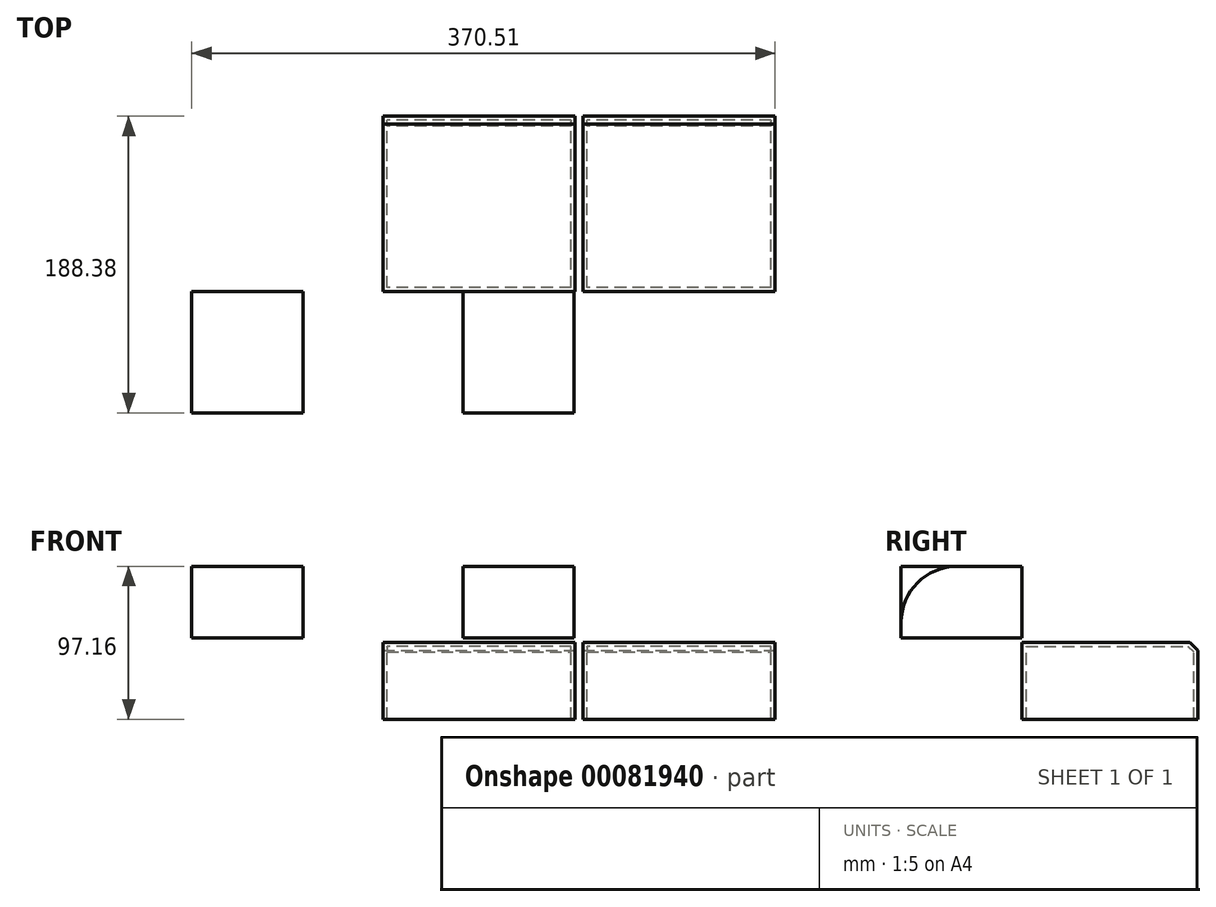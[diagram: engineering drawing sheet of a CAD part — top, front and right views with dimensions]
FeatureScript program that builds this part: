
annotation { "Feature Type Name" : "Feature", "Feature Type Description" : "" }
export const myFeature = defineFeature(function(context is Context, id is Id, definition is map)
    precondition{}
    {
        {
            var Q0;
            Q0=qCreatedBy(makeId("Right.planeOp"),FACE);
            var sketch = newSketch(context, id + "F0", { "sketchPlane" : qUnion([Q0])});
            skLineSegment(sketch, "E0.bottom", {"start": v(0, 0) * mm, "end": v(111.46, 0) * mm});
            skLineSegment(sketch, "E0.top", {"start": v(0, 48.95) * mm, "end": v(111.46, 48.95) * mm});
            skLineSegment(sketch, "E0.left", {"start": v(0, 0) * mm, "end": v(0, 48.95) * mm});
            skLineSegment(sketch, "E0.right", {"start": v(111.46, 0) * mm, "end": v(111.46, 48.95) * mm});
            skSolve(sketch);
        }
        {
            var Q0;
            Q0=qSketchRegion(id+"F0",true);
            extrude(context, id + "F1", {"entities" : qUnion([Q0]), "depth" : 122.06 * mm});
        }
        {
            var Q0;
            Q0=makeQuery(id+"F1.opExtrude","SWEPT_EDGE",EDGE,{"disambiguationData":[OSD([sQuery(id+"F0.wireOp",EDGE,"E0.top"),sQuery(id+"F0.wireOp",EDGE,"E0.right")])]});
            chamfer(context, id + "F2", {"entities" : qUnion([Q0]), "width" : 5.08 * mm, "tangentPropagation" : true});
        }
        {
            var Q0;
            Q0=makeQuery(id+"F1.opExtrude","SWEPT_FACE",FACE,{"disambiguationData":[OSD([sQuery(id+"F0.wireOp",EDGE,"E0.bottom")])]});
            shell(context, id + "F3", {"entities" : qUnion([Q0]), "thickness" : 2.54 * mm});
        }
        {
            var Q0;
            Q0=qCreatedBy(makeId("Front.planeOp"),FACE);
            var sketch = newSketch(context, id + "F4", { "sketchPlane" : qUnion([Q0])});
            skLineSegment(sketch, "E1.bottom", {"start": v(-50.88, 51.58) * mm, "end": v(-121.45, 51.58) * mm});
            skLineSegment(sketch, "E1.top", {"start": v(-50.88, 97.16) * mm, "end": v(-121.45, 97.16) * mm});
            skLineSegment(sketch, "E1.left", {"start": v(-50.88, 51.58) * mm, "end": v(-50.88, 97.16) * mm});
            skLineSegment(sketch, "E1.right", {"start": v(-121.45, 51.58) * mm, "end": v(-121.45, 97.16) * mm});
            skSolve(sketch);
        }
        {
            var Q0;
            Q0=makeQuery(id+"F4.imprint","IMPRINT",FACE,{"disambiguationData":[TD([[makeQuery(id+"F4.imprint","IMPRINT",EDGE,{"derivedFrom":sQuery(id+"F4.wireOp",EDGE,"E1.bottom")}),-1.0]])]});
            extrude(context, id + "F5", {"entities" : qUnion([Q0]), "depth" : 76.92 * mm});
        }
        {
            var Q0;
            Q0=makeQuery(id+"F5.opExtrude","SWEPT_BODY",BODY,{"disambiguationData":[OSD([sQuery(id+"F4.wireOp",EDGE,"E1.bottom"),sQuery(id+"F4.wireOp",EDGE,"E1.top"),sQuery(id+"F4.wireOp",EDGE,"E1.left"),sQuery(id+"F4.wireOp",EDGE,"E1.right")])]});
            var Q1;
            Q1=qCreatedBy(makeId("Right.planeOp"),FACE);
            mirror(context, id + "F6", {"entities" : qUnion([Q0]), "mirrorPlane" : qUnion([Q1])});
        }
        {
            var Q0;
            Q0=makeQuery(id+"F1.opExtrude","SWEPT_BODY",BODY,{"disambiguationData":[OSD([sQuery(id+"F0.wireOp",EDGE,"E0.bottom"),sQuery(id+"F0.wireOp",EDGE,"E0.top"),sQuery(id+"F0.wireOp",EDGE,"E0.left"),sQuery(id+"F0.wireOp",EDGE,"E0.right")])]});
            transform(context, id + "F7", {"entities" : qUnion([Q0]), "transformType" : TransformType.TRANSLATION_3D, "dx" : 127 * mm, "dy" : 0 * mm, "dz" : 0 * mm, "makeCopy" : true});
        }
        {
            var Q0;
            Q0=makeQuery(id+"F6.opPattern","COPY",EDGE,{"derivedFrom":makeQuery(id+"F5.opExtrude","CAP_EDGE",EDGE,{"disambiguationData":[OSD([sQuery(id+"F4.wireOp",EDGE,"E1.top")])],"isStart":false}),"instanceName":"1"});
            fillet(context, id + "F8", {"entities" : qUnion([Q0]), "radius" : 35.65 * mm, "tangentPropagation" : true, "allowEdgeOverflow" : false});
        }
    });
